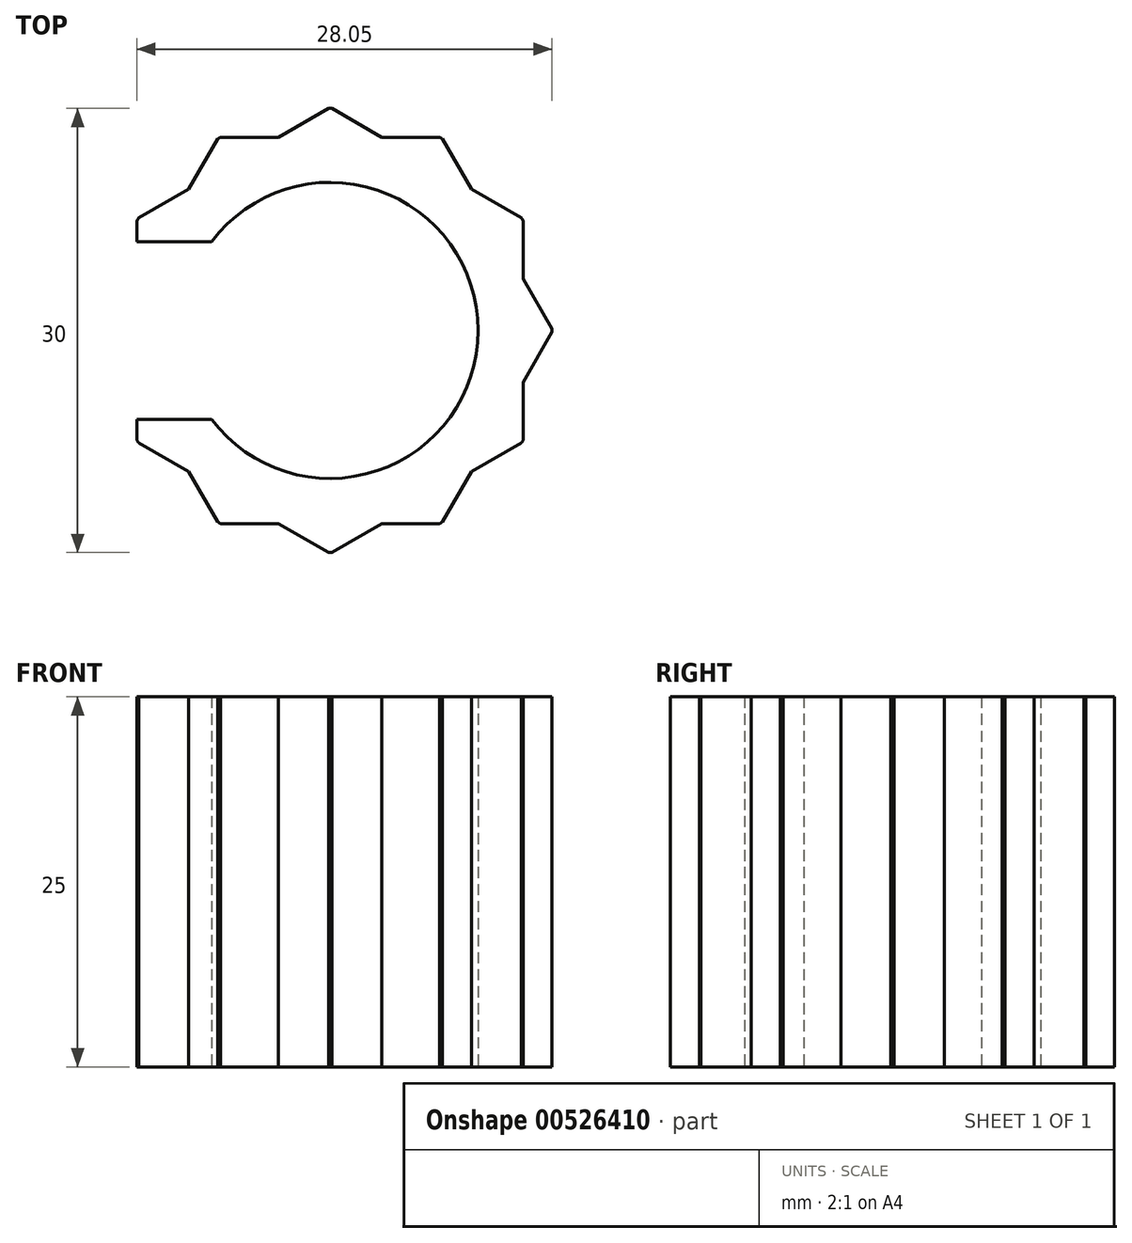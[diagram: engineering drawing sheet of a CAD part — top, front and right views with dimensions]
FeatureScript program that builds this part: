
annotation { "Feature Type Name" : "Feature", "Feature Type Description" : "" }
export const myFeature = defineFeature(function(context is Context, id is Id, definition is map)
    precondition{}
    {
        {
            var Q0;
            Q0=qCreatedBy(makeId("Top.planeOp"),FACE);
            var sketch = newSketch(context, id + "F0", { "sketchPlane" : qUnion([Q0])});
            skCircle(sketch, "E0", {"center": v(0, 0) * mm, "radius": 15 * mm});
            skCircle(sketch, "E1.cCircle", {"center": v(0, 0) * mm, "radius": 13.05 * mm, "construction": true});
            skLineSegment(sketch, "E1.0", {"start": v(0, 15.06) * mm, "end": v(3.5, 13.05) * mm});
            skLineSegment(sketch, "E1.1", {"start": v(13.05, 7.53) * mm, "end": v(13.05, 3.5) * mm});
            skLineSegment(sketch, "E1.2", {"start": v(13.05, -7.53) * mm, "end": v(9.55, -9.55) * mm});
            skLineSegment(sketch, "E1.3", {"start": v(0, -15.06) * mm, "end": v(-3.5, -13.05) * mm});
            skLineSegment(sketch, "E1.4", {"start": v(-13.05, -7.53) * mm, "end": v(-13.05, -3.5) * mm});
            skLineSegment(sketch, "E1.5", {"start": v(-13.05, 7.53) * mm, "end": v(-9.55, 9.55) * mm});
            skPoint(sketch, "E1.0.midPoint", {"position": v(6.52, 11.3) * mm});
            skLineSegment(sketch, "E2.0", {"start": v(-7.53, 13.05) * mm, "end": v(-3.5, 13.05) * mm});
            skLineSegment(sketch, "E2.1", {"start": v(7.53, 13.05) * mm, "end": v(9.55, 9.55) * mm});
            skLineSegment(sketch, "E2.2", {"start": v(15.06, 0) * mm, "end": v(13.05, -3.5) * mm});
            skLineSegment(sketch, "E2.3", {"start": v(7.53, -13.05) * mm, "end": v(3.5, -13.05) * mm});
            skLineSegment(sketch, "E2.4", {"start": v(-7.53, -13.05) * mm, "end": v(-9.55, -9.55) * mm});
            skLineSegment(sketch, "E2.5", {"start": v(-15.06, 0) * mm, "end": v(-13.05, 3.5) * mm});
            skPoint(sketch, "E2.0.midPoint", {"position": v(0, 13.05) * mm});
            skLineSegment(sketch, "E3.trimOffspring", {"start": v(-3.5, 13.05) * mm, "end": v(0, 15.06) * mm});
            skLineSegment(sketch, "E4.trimOffspring", {"start": v(3.5, 13.05) * mm, "end": v(7.53, 13.05) * mm});
            skLineSegment(sketch, "E5.trimOffspring", {"start": v(9.55, 9.55) * mm, "end": v(13.05, 7.53) * mm});
            skLineSegment(sketch, "E6.trimOffspring", {"start": v(13.05, 3.5) * mm, "end": v(15.06, 0) * mm});
            skLineSegment(sketch, "E7.trimOffspring", {"start": v(13.05, -3.5) * mm, "end": v(13.05, -7.53) * mm});
            skLineSegment(sketch, "E8.trimOffspring", {"start": v(9.55, -9.55) * mm, "end": v(7.53, -13.05) * mm});
            skLineSegment(sketch, "E9.trimOffspring", {"start": v(3.5, -13.05) * mm, "end": v(0, -15.06) * mm});
            skLineSegment(sketch, "E10.trimOffspring", {"start": v(-3.5, -13.05) * mm, "end": v(-7.53, -13.05) * mm});
            skLineSegment(sketch, "E11.trimOffspring", {"start": v(-9.55, -9.55) * mm, "end": v(-13.05, -7.53) * mm});
            skLineSegment(sketch, "E12.trimOffspring", {"start": v(-13.05, -3.5) * mm, "end": v(-15.06, 0) * mm});
            skLineSegment(sketch, "E13.trimOffspring", {"start": v(-13.05, 3.5) * mm, "end": v(-13.05, 7.53) * mm});
            skLineSegment(sketch, "E14.trimOffspring", {"start": v(-9.55, 9.55) * mm, "end": v(-7.53, 13.05) * mm});
            skLineSegment(sketch, "E15", {"start": v(-8, 6) * mm, "end": v(-24, 6) * mm});
            skLineSegment(sketch, "E16", {"start": v(-24, 6) * mm, "end": v(-24, -6) * mm});
            skLineSegment(sketch, "E17", {"start": v(-24, -6) * mm, "end": v(-8, -6) * mm});
            skLineSegment(sketch, "E18", {"start": v(-8, -6) * mm, "end": v(-8, 6) * mm});
            skCircle(sketch, "E19.0", {"center": v(0, 0) * mm, "radius": 10 * mm});
            skSolve(sketch);
        }
        {
            var Q0;
            {var subQ1=sQuery(id+"F0.wireOp",EDGE,"E0");var subQ17=sQuery(id+"F0.wireOp",EDGE,"E1.1");var subQ19=makeQuery(id+"F0.imprint","INTERSECT",VERTEX,{"derivedFrom":[subQ1,subQ17]});Q0=makeQuery(id+"F0.imprint","IMPRINT",FACE,{"disambiguationData":[TD([[makeQuery(id+"F0.imprint","IMPRINT",EDGE,{"disambiguationData":[TD([[subQ19,-1.0]])],"derivedFrom":subQ1}),1.0]])]});}
            extrude(context, id + "F1", {"entities" : qUnion([Q0]), "endBound" : BoundingType.SYMMETRIC, "depth" : 25 * mm, "offsetDistance" : 25 * mm});
        }
    });
